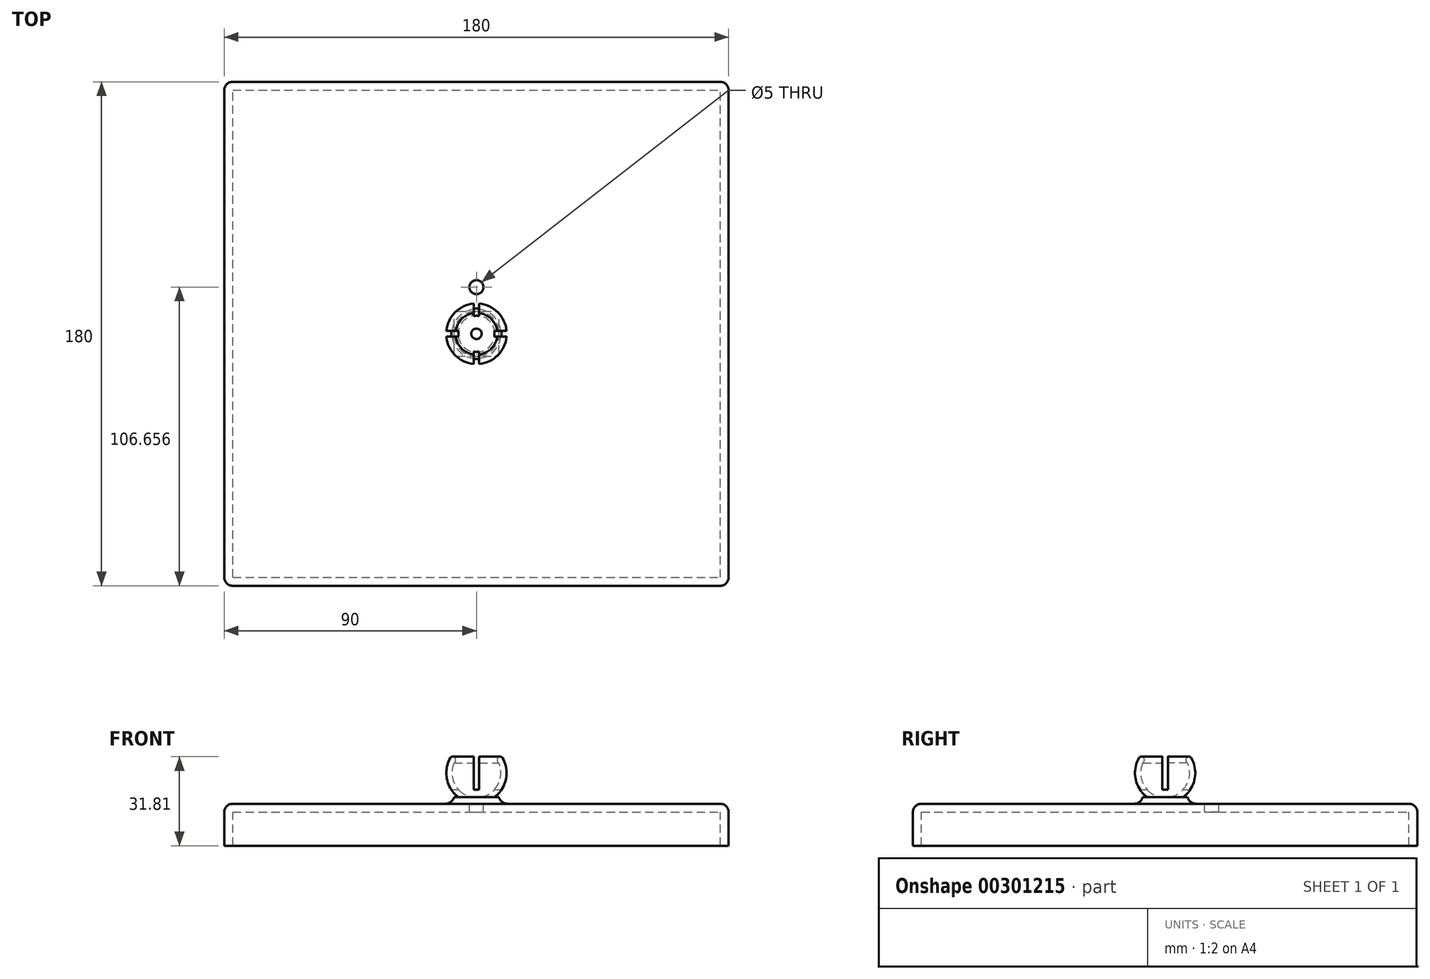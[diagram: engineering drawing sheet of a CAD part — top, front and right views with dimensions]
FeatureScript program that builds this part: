
annotation { "Feature Type Name" : "Feature", "Feature Type Description" : "" }
export const myFeature = defineFeature(function(context is Context, id is Id, definition is map)
    precondition{}
    {
        {
            var Q0;
            Q0=qCreatedBy(makeId("Front.planeOp"),FACE);
            var sketch = newSketch(context, id + "F0", { "sketchPlane" : qUnion([Q0])});
            skArc(sketch, "E0", {"start": v(0, -8.8) * mm, "mid": v(7.36, -4.83) * mm, "end": v(8.07, 3.5) * mm});
            skArc(sketch, "E1", {"start": v(9.06, 5.87) * mm, "mid": v(7.56, 5.11) * mm, "end": v(8.07, 3.5) * mm});
            skArc(sketch, "E2", {"start": v(0, -10.8) * mm, "mid": v(9.49, -5.16) * mm, "end": v(9.06, 5.87) * mm});
            skLineSegment(sketch, "E3.trimOffspring", {"start": v(0, -8.8) * mm, "end": v(0, -10.8) * mm});
            skLineSegment(sketch, "E4", {"start": v(0, 12.43) * mm, "end": v(0, -22.9) * mm});
            skSolve(sketch);
        }
        {
            var Q0;
            {var subQ0=sQuery(id+"F0.wireOp",EDGE,"E0");Q0=makeQuery(id+"F0.imprint","IMPRINT",FACE,{"disambiguationData":[TD([[makeQuery(id+"F0.imprint","IMPRINT",EDGE,{"derivedFrom":subQ0}),-1.0]])]});}
            var Q1;
            Q1=sQuery(id+"F0.wireOp",EDGE,"E4");
            revolve(context, id + "F1", {"entities" : qUnion([Q0]), "axis" : qUnion([Q1]), "revolveType" : RevolveType.FULL});
        }
        {
            var Q0;
            Q0=makeQuery(id+"F1.opRevolve","SWEPT_EDGE",EDGE,{"disambiguationData":[OSD([sQuery(id+"F0.wireOp",EDGE,"E1"),sQuery(id+"F0.wireOp",EDGE,"E2")])]});
            fillet(context, id + "F2", {"entities" : qUnion([Q0]), "radius" : 1 * mm, "tangentPropagation" : true, "allowEdgeOverflow" : false});
        }
        {
            var Q0;
            Q0=qCreatedBy(makeId("Top.planeOp"),FACE);
            var sketch = newSketch(context, id + "F3", { "sketchPlane" : qUnion([Q0])});
            skLineSegment(sketch, "E5.bottom", {"start": v(0, -14.6) * mm, "end": v(1, -14.6) * mm});
            skLineSegment(sketch, "E5.top", {"start": v(0, 15.05) * mm, "end": v(1, 15.05) * mm});
            skLineSegment(sketch, "E5.left", {"start": v(0, -14.6) * mm, "end": v(0, 15.05) * mm});
            skLineSegment(sketch, "E5.right", {"start": v(1, -14.6) * mm, "end": v(1, 15.05) * mm});
            skLineSegment(sketch, "E6.bottom", {"start": v(-15.47, 0) * mm, "end": v(18.42, 0) * mm});
            skLineSegment(sketch, "E6.top", {"start": v(-15.47, 1) * mm, "end": v(18.42, 1) * mm});
            skLineSegment(sketch, "E6.left", {"start": v(-15.47, 0) * mm, "end": v(-15.47, 1) * mm});
            skLineSegment(sketch, "E6.right", {"start": v(18.42, 0) * mm, "end": v(18.42, 1) * mm});
            skLineSegment(sketch, "E7.bottom", {"start": v(0, -14.6) * mm, "end": v(-1, -14.6) * mm});
            skLineSegment(sketch, "E7.top", {"start": v(0, 15.05) * mm, "end": v(-1, 15.05) * mm});
            skLineSegment(sketch, "E7.right", {"start": v(-1, -14.6) * mm, "end": v(-1, 15.05) * mm});
            skLineSegment(sketch, "E8.top", {"start": v(-15.47, -1) * mm, "end": v(18.42, -1) * mm});
            skLineSegment(sketch, "E8.left", {"start": v(-15.47, 0) * mm, "end": v(-15.47, -1) * mm});
            skLineSegment(sketch, "E8.right", {"start": v(18.42, 0) * mm, "end": v(18.42, -1) * mm});
            skSolve(sketch);
        }
        {
            var Q0;
            {var subQ0=sQuery(id+"F3.wireOp",EDGE,"E5.bottom");Q0=makeQuery(id+"F3.imprint","IMPRINT",FACE,{"disambiguationData":[TD([[makeQuery(id+"F3.imprint","IMPRINT",EDGE,{"derivedFrom":subQ0}),1.0]])]});}
            var Q1;
            {var subQ0=sQuery(id+"F3.wireOp",EDGE,"E7.bottom");Q1=makeQuery(id+"F3.imprint","IMPRINT",FACE,{"disambiguationData":[TD([[makeQuery(id+"F3.imprint","IMPRINT",EDGE,{"derivedFrom":subQ0}),-1.0]])]});}
            var Q2;
            {var subQ5=sQuery(id+"F3.wireOp",EDGE,"E8.left");Q2=makeQuery(id+"F3.imprint","IMPRINT",FACE,{"disambiguationData":[TD([[makeQuery(id+"F3.imprint","IMPRINT",EDGE,{"derivedFrom":subQ5}),1.0]])]});}
            var Q3;
            {var subQ0=sQuery(id+"F3.wireOp",EDGE,"E6.left");Q3=makeQuery(id+"F3.imprint","IMPRINT",FACE,{"disambiguationData":[TD([[makeQuery(id+"F3.imprint","IMPRINT",EDGE,{"derivedFrom":subQ0}),-1.0]])]});}
            var Q4;
            {var subQ5=sQuery(id+"F3.wireOp",EDGE,"E7.top");Q4=makeQuery(id+"F3.imprint","IMPRINT",FACE,{"disambiguationData":[TD([[makeQuery(id+"F3.imprint","IMPRINT",EDGE,{"derivedFrom":subQ5}),1.0]])]});}
            var Q5;
            {var subQ5=sQuery(id+"F3.wireOp",EDGE,"E8.right");Q5=makeQuery(id+"F3.imprint","IMPRINT",FACE,{"disambiguationData":[TD([[makeQuery(id+"F3.imprint","IMPRINT",EDGE,{"derivedFrom":subQ5}),-1.0]])]});}
            var Q6;
            {var subQ5=sQuery(id+"F3.wireOp",EDGE,"E6.right");Q6=makeQuery(id+"F3.imprint","IMPRINT",FACE,{"disambiguationData":[TD([[makeQuery(id+"F3.imprint","IMPRINT",EDGE,{"derivedFrom":subQ5}),1.0]])]});}
            var Q7;
            {var subQ0=sQuery(id+"F3.wireOp",EDGE,"E5.top");Q7=makeQuery(id+"F3.imprint","IMPRINT",FACE,{"disambiguationData":[TD([[makeQuery(id+"F3.imprint","IMPRINT",EDGE,{"derivedFrom":subQ0}),-1.0]])]});}
            extrude(context, id + "F4", {"entities" : qUnion([Q0, Q1, Q2, Q3, Q4, Q5, Q6, Q7]), "operationType" : NewBodyOperationType.REMOVE, "oppositeDirection" : true, "depth" : 6 * mm, "hasSecondDirection" : true, "secondDirectionOppositeDirection" : false, "secondDirectionDepth" : 6 * mm});
        }
        {
            var Q0;
            Q0=qCreatedBy(makeId("Top.planeOp"),FACE);
            cPlane(context, id + "F5", {"entities" : qUnion([Q0]), "cplaneType" : CPlaneType.OFFSET, "offset" : 11 * mm, "oppositeDirection" : true, "width" : 150 * mm, "height" : 150 * mm});
        }
        {
            var Q0;
            Q0=qCreatedBy(id+"F5.planeOp",FACE);
            var sketch = newSketch(context, id + "F6", { "sketchPlane" : qUnion([Q0])});
            skLineSegment(sketch, "E9.bottom", {"start": v(-8, -8) * mm, "end": v(8, -8) * mm});
            skLineSegment(sketch, "E9.top", {"start": v(-8, 8) * mm, "end": v(8, 8) * mm});
            skLineSegment(sketch, "E9.left", {"start": v(-8, -8) * mm, "end": v(-8, 8) * mm});
            skLineSegment(sketch, "E9.right", {"start": v(8, -8) * mm, "end": v(8, 8) * mm});
            skSolve(sketch);
        }
        {
            var Q0;
            Q0=makeQuery(id+"F6.imprint","IMPRINT",FACE,{"disambiguationData":[TD([[makeQuery(id+"F6.imprint","IMPRINT",EDGE,{"derivedFrom":sQuery(id+"F6.wireOp",EDGE,"E9.bottom")}),1.0]])]});
            extrude(context, id + "F7", {"entities" : qUnion([Q0]), "operationType" : NewBodyOperationType.ADD, "depth" : 2.4 * mm});
        }
        {
            var Q0;
            Q0=makeQuery(id+"F7.opExtrude","SWEPT_EDGE",EDGE,{"disambiguationData":[OSD([sQuery(id+"F6.wireOp",EDGE,"E9.bottom"),sQuery(id+"F6.wireOp",EDGE,"E9.left")])]});
            var Q1;
            Q1=makeQuery(id+"F7.opExtrude","SWEPT_EDGE",EDGE,{"disambiguationData":[OSD([sQuery(id+"F6.wireOp",EDGE,"E9.top"),sQuery(id+"F6.wireOp",EDGE,"E9.left")])]});
            var Q2;
            Q2=makeQuery(id+"F7.opExtrude","SWEPT_EDGE",EDGE,{"disambiguationData":[OSD([sQuery(id+"F6.wireOp",EDGE,"E9.bottom"),sQuery(id+"F6.wireOp",EDGE,"E9.right")])]});
            var Q3;
            Q3=makeQuery(id+"F7.opExtrude","SWEPT_EDGE",EDGE,{"disambiguationData":[OSD([sQuery(id+"F6.wireOp",EDGE,"E9.top"),sQuery(id+"F6.wireOp",EDGE,"E9.right")])]});
            fillet(context, id + "F8", {"entities" : qUnion([Q0, Q1, Q2, Q3]), "radius" : 1 * mm, "tangentPropagation" : true, "allowEdgeOverflow" : false});
        }
        {
            var Q0;
            Q0=makeQuery(id+"F7.opExtrude","CAP_FACE",FACE,{"disambiguationData":[OSD([sQuery(id+"F6.wireOp",EDGE,"E9.bottom"),sQuery(id+"F6.wireOp",EDGE,"E9.top"),sQuery(id+"F6.wireOp",EDGE,"E9.left"),sQuery(id+"F6.wireOp",EDGE,"E9.right")])],"isStart":true});
            var sketch = newSketch(context, id + "F9", { "sketchPlane" : qUnion([Q0])});
            skLineSegment(sketch, "E10.bottom", {"start": v(-90, 90) * mm, "end": v(90, 90) * mm});
            skLineSegment(sketch, "E10.top", {"start": v(-90, -90) * mm, "end": v(90, -90) * mm});
            skLineSegment(sketch, "E10.left", {"start": v(-90, 90) * mm, "end": v(-90, -90) * mm});
            skLineSegment(sketch, "E10.right", {"start": v(90, 90) * mm, "end": v(90, -90) * mm});
            skLineSegment(sketch, "E11.bottom", {"start": v(87, -87) * mm, "end": v(-87, -87) * mm});
            skLineSegment(sketch, "E11.top", {"start": v(87, 87) * mm, "end": v(-87, 87) * mm});
            skLineSegment(sketch, "E11.left", {"start": v(87, -87) * mm, "end": v(87, 87) * mm});
            skLineSegment(sketch, "E11.right", {"start": v(-87, -87) * mm, "end": v(-87, 87) * mm});
            skPoint(sketch, "E11.middle", {"position": v(0, 0) * mm});
            skSolve(sketch);
        }
        {
            var Q0;
            Q0=makeQuery(id+"F9.imprint","IMPRINT",FACE,{"disambiguationData":[TD([[makeQuery(id+"F9.imprint","IMPRINT",EDGE,{"derivedFrom":sQuery(id+"F9.wireOp",EDGE,"E10.bottom")}),-1.0]])]});
            var Q1;
            {var subQ3=sQuery(id+"F6.wireOp",EDGE,"E9.bottom");Q1=makeQuery(id+"F9.imprint","IMPRINT",FACE,{"disambiguationData":[TD([[makeQuery(id+"F9.imprint","IMPRINT",EDGE,{"derivedFrom":makeQuery(id+"F7.opExtrude","CAP_EDGE",EDGE,{"disambiguationData":[OSD([subQ3])],"isStart":true})}),-1.0]])]});}
            var Q2;
            Q2=makeQuery(id+"F9.imprint","IMPRINT",FACE,{"disambiguationData":[TD([[makeQuery(id+"F9.imprint","IMPRINT",EDGE,{"derivedFrom":sQuery(id+"F9.wireOp",EDGE,"E11.bottom")}),-1.0]])]});
            extrude(context, id + "F10", {"entities" : qUnion([Q0, Q1, Q2]), "operationType" : NewBodyOperationType.ADD, "depth" : 3 * mm});
        }
        {
            var Q0;
            Q0=makeQuery(id+"F9.imprint","IMPRINT",FACE,{"disambiguationData":[TD([[makeQuery(id+"F9.imprint","IMPRINT",EDGE,{"derivedFrom":sQuery(id+"F9.wireOp",EDGE,"E10.bottom")}),-1.0]])]});
            extrude(context, id + "F11", {"entities" : qUnion([Q0]), "operationType" : NewBodyOperationType.ADD, "depth" : 15 * mm});
        }
        {
            var Q0;
            {var subQ0=sQuery(id+"F9.wireOp",EDGE,"E10.left");var subQ1=sQuery(id+"F9.wireOp",EDGE,"E10.top");Q0=makeQuery(id+"F11.boolean.opBoolean","MERGE",EDGE,{"derivedFrom":[makeQuery(id+"F10.opExtrude","SWEPT_EDGE",EDGE,{"disambiguationData":[OSD([subQ1,subQ0])]}),makeQuery(id+"F11.opExtrude","SWEPT_EDGE",EDGE,{"disambiguationData":[OSD([subQ1,subQ0])]})]});}
            var Q1;
            {var subQ0=sQuery(id+"F9.wireOp",EDGE,"E10.right");var subQ1=sQuery(id+"F9.wireOp",EDGE,"E10.top");Q1=makeQuery(id+"F11.boolean.opBoolean","MERGE",EDGE,{"derivedFrom":[makeQuery(id+"F10.opExtrude","SWEPT_EDGE",EDGE,{"disambiguationData":[OSD([subQ1,subQ0])]}),makeQuery(id+"F11.opExtrude","SWEPT_EDGE",EDGE,{"disambiguationData":[OSD([subQ1,subQ0])]})]});}
            var Q2;
            {var subQ0=sQuery(id+"F9.wireOp",EDGE,"E10.right");var subQ1=sQuery(id+"F9.wireOp",EDGE,"E10.bottom");Q2=makeQuery(id+"F11.boolean.opBoolean","MERGE",EDGE,{"derivedFrom":[makeQuery(id+"F10.opExtrude","SWEPT_EDGE",EDGE,{"disambiguationData":[OSD([subQ1,subQ0])]}),makeQuery(id+"F11.opExtrude","SWEPT_EDGE",EDGE,{"disambiguationData":[OSD([subQ1,subQ0])]})]});}
            var Q3;
            {var subQ0=sQuery(id+"F9.wireOp",EDGE,"E10.left");var subQ1=sQuery(id+"F9.wireOp",EDGE,"E10.bottom");Q3=makeQuery(id+"F11.boolean.opBoolean","MERGE",EDGE,{"derivedFrom":[makeQuery(id+"F10.opExtrude","SWEPT_EDGE",EDGE,{"disambiguationData":[OSD([subQ1,subQ0])]}),makeQuery(id+"F11.opExtrude","SWEPT_EDGE",EDGE,{"disambiguationData":[OSD([subQ1,subQ0])]})]});}
            var Q4;
            Q4=makeQuery(id+"F10.opExtrude","CAP_FACE",FACE,{"disambiguationData":[OSD([sQuery(id+"F9.wireOp",EDGE,"E10.bottom"),sQuery(id+"F9.wireOp",EDGE,"E10.top"),sQuery(id+"F9.wireOp",EDGE,"E10.left"),sQuery(id+"F9.wireOp",EDGE,"E10.right")])],"isStart":true});
            fillet(context, id + "F12", {"entities" : qUnion([Q0, Q1, Q2, Q3, Q4]), "radius" : 3 * mm, "tangentPropagation" : true, "allowEdgeOverflow" : false});
        }
        {
            var Q0;
            Q0=makeQuery(id+"F9.imprint","IMPRINT",FACE,{"disambiguationData":[TD([[makeQuery(id+"F9.imprint","IMPRINT",EDGE,{"derivedFrom":sQuery(id+"F9.wireOp",EDGE,"E11.bottom")}),-1.0]])]});
            var sketch = newSketch(context, id + "F13", { "sketchPlane" : qUnion([Q0])});
            skCircle(sketch, "E12", {"center": v(0, -16.66) * mm, "radius": 2.5 * mm});
            skSolve(sketch);
        }
        {
            var Q0;
            Q0=makeQuery(id+"F13.imprint","IMPRINT",FACE,{"disambiguationData":[TD([[makeQuery(id+"F13.imprint","IMPRINT",EDGE,{"derivedFrom":sQuery(id+"F13.wireOp",EDGE,"E12")}),1.0]])]});
            extrude(context, id + "F14", {"entities" : qUnion([Q0]), "operationType" : NewBodyOperationType.REMOVE, "depth" : 25 * mm});
        }
    });
